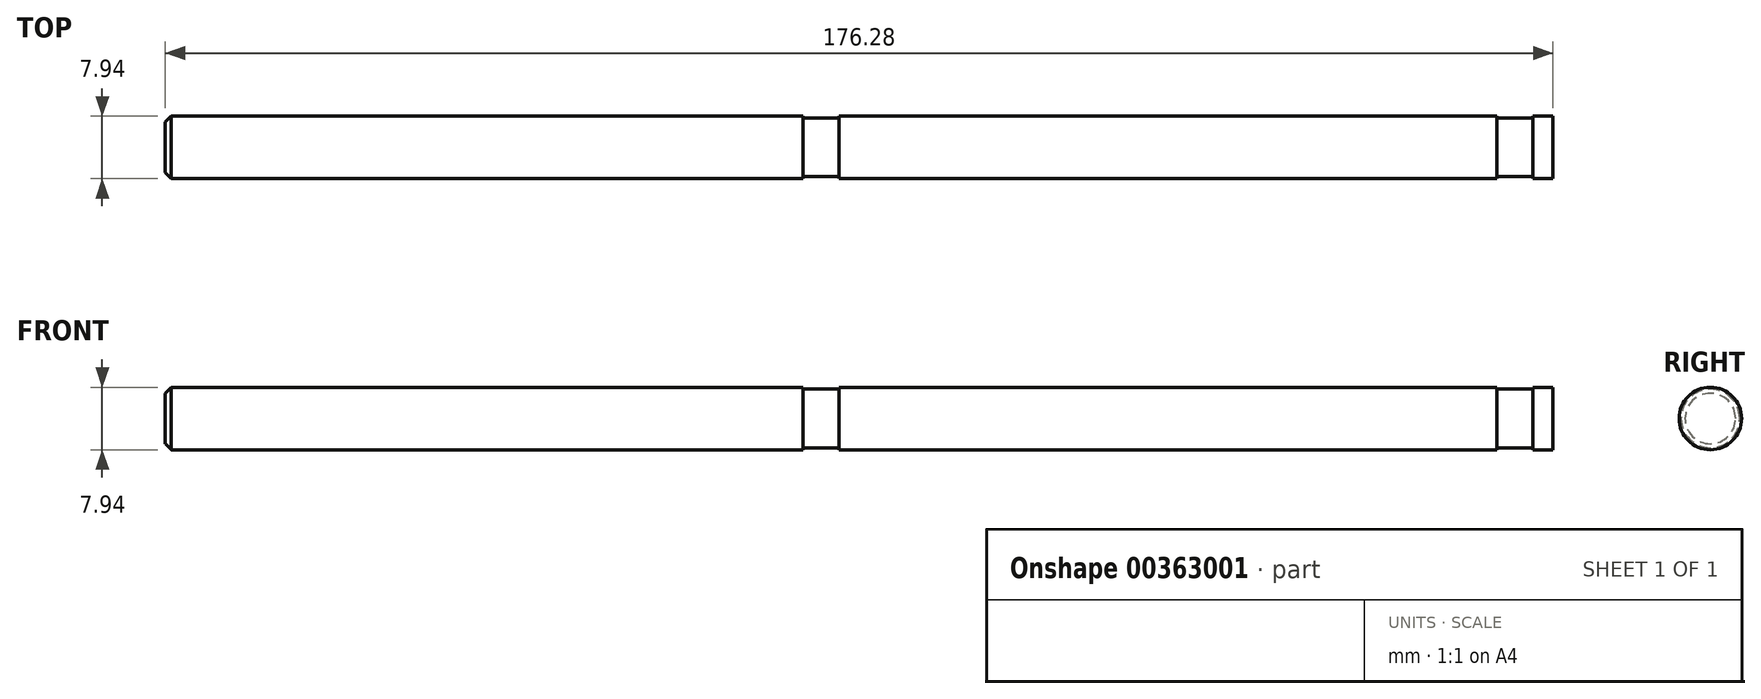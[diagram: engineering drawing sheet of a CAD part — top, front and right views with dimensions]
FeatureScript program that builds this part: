
annotation { "Feature Type Name" : "Feature", "Feature Type Description" : "" }
export const myFeature = defineFeature(function(context is Context, id is Id, definition is map)
    precondition{}
    {
        {
            var Q0;
            Q0=qCreatedBy(makeId("Right.planeOp"),FACE);
            var sketch = newSketch(context, id + "F0", { "sketchPlane" : qUnion([Q0])});
            skCircle(sketch, "E0", {"center": v(0, 0) * mm, "radius": 3.97 * mm});
            skSolve(sketch);
        }
        {
            var Q0;
            Q0 = qSketchRegion(id + "F0", true);
            extrude(context, id + "F1", {"entities" : qUnion([Q0]), "depth" : 176.28 * mm});
        }
        {
            var Q0;
            Q0=qCreatedBy(makeId("Front.planeOp"),FACE);
            var sketch = newSketch(context, id + "F2", { "sketchPlane" : qUnion([Q0])});
            skLineSegment(sketch, "E1.0", {"start": v(173.74, 5.42) * mm, "end": v(173.74, 3.72) * mm});
            skLineSegment(sketch, "E2.0", {"start": v(169.16, 5.42) * mm, "end": v(169.16, 3.72) * mm});
            skLineSegment(sketch, "E3", {"start": v(173.74, 0) * mm, "end": v(169.16, 0) * mm});
            skLineSegment(sketch, "E4.0", {"start": v(173.74, 3.72) * mm, "end": v(169.16, 3.72) * mm});
            skLineSegment(sketch, "E5", {"start": v(169.16, 5.42) * mm, "end": v(173.74, 5.42) * mm});
            skPoint(sketch, "E6.orphan", {"position": v(175.5, 0) * mm});
            skLineSegment(sketch, "E7.0", {"start": v(85.6, 5.42) * mm, "end": v(85.6, 3.72) * mm});
            skLineSegment(sketch, "E8.0", {"start": v(81.03, 5.42) * mm, "end": v(81.03, 3.72) * mm});
            skLineSegment(sketch, "E9.0", {"start": v(85.6, 3.72) * mm, "end": v(81.03, 3.72) * mm});
            skLineSegment(sketch, "E10", {"start": v(81.03, 5.42) * mm, "end": v(85.6, 5.42) * mm});
            skSolve(sketch);
        }
        {
            var Q0;
            Q0=makeQuery(id+"F2.imprint","IMPRINT",FACE,{"disambiguationData":[TD([[makeQuery(id+"F2.imprint","IMPRINT",EDGE,{"derivedFrom":sQuery(id+"F2.wireOp",EDGE,"E1.0")}),-1.0]])]});
            var Q1;
            Q1=makeQuery(id+"F2.imprint","IMPRINT",FACE,{"disambiguationData":[TD([[makeQuery(id+"F2.imprint","IMPRINT",EDGE,{"derivedFrom":sQuery(id+"F2.wireOp",EDGE,"E7.0")}),-1.0]])]});
            var Q2;
            Q2=sQuery(id+"F2.wireOp",EDGE,"E3");
            revolve(context, id + "F3", {"operationType" : NewBodyOperationType.REMOVE, "entities" : qUnion([Q0, Q1]), "axis" : qUnion([Q2]), "revolveType" : RevolveType.FULL, "oppositeDirection" : true});
        }
        {
            var Q0;
            Q0=makeQuery(id+"F1.opExtrude","CAP_EDGE",EDGE,{"disambiguationData":[OSD([sQuery(id+"F0.wireOp",EDGE,"E0")])],"isStart":true});
            chamfer(context, id + "F4", {"entities" : qUnion([Q0]), "chamferType" : ChamferType.OFFSET_ANGLE, "width" : 0.76 * mm, "oppositeDirection" : false, "angle" : 45 * degree, "tangentPropagation" : true});
        }
    });
